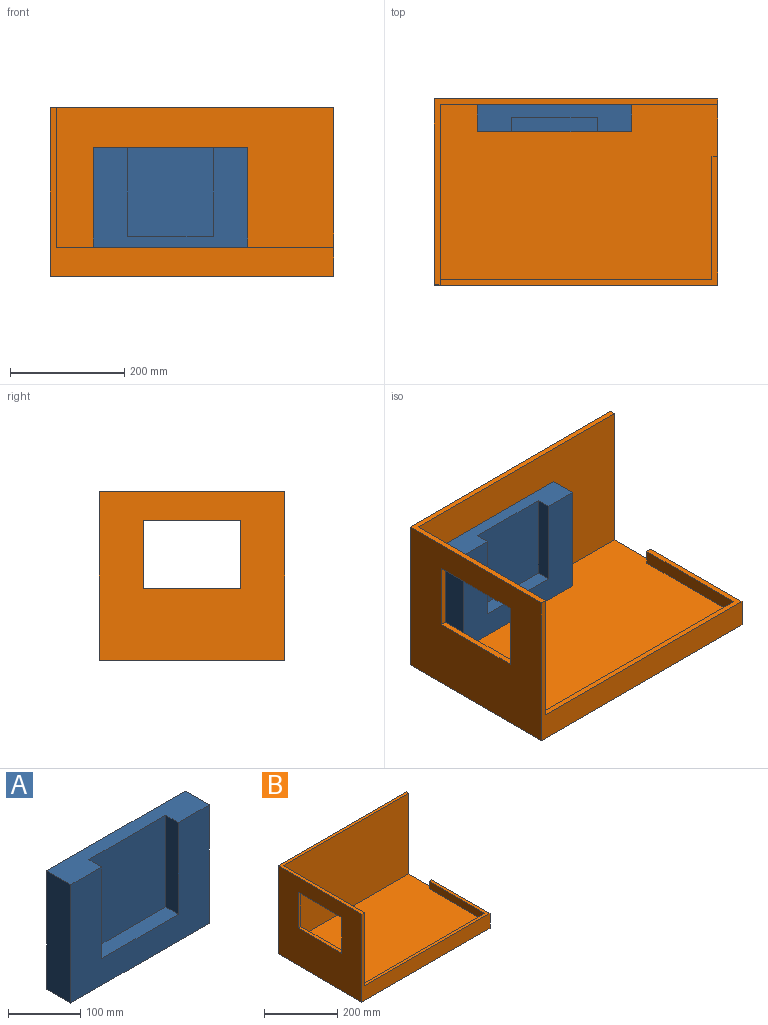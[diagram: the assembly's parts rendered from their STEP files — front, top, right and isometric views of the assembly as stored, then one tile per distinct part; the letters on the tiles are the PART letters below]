
ASSEMBLY  parts=2 mates=2
PART A: 10 faces, bbox 270x47x200 mm
  f0: plane 270x200mm, normal (0,-1,0), area 30750mm2, adj f1,f2,f4,f5,f6,f7,f8
  f1: plane 270x47mm, normal (0,0,1), area 8940mm2, adj f0,f2,f3,f4,f6,f8,f9
  f2: plane 200x47mm, normal (1,0,0), area 9400mm2, adj f0,f1,f3,f5
  f3: plane 270x200mm, normal (0,1,0), area 54000mm2, adj f1,f2,f4,f5
  f4: plane 200x47mm, normal (-1,0,0), area 9400mm2, adj f0,f1,f3,f5
  f5: plane 270x47mm, normal (0,0,-1), area 12690mm2, adj f0,f2,f3,f4
  f6: plane 155x25mm, normal (1,0,0), area 3875mm2, adj f0,f1,f7,f9
  f7: plane 150x25mm, normal (0,0,1), area 3750mm2, adj f0,f6,f8,f9
  f8: plane 155x25mm, normal (-1,0,0), area 3875mm2, adj f0,f1,f7,f9
  f9: plane 155x150mm, normal (0,-1,0), area 23250mm2, adj f1,f6,f7,f8
PART B: 17 faces, bbox 495.6x325x295 mm
  f0: plane 315x270mm, normal (1,0,0), area 64400mm2, adj f3,f4,f7,f10,f11,f12,f13,f14
  f1: plane 325x295mm, normal (-1,0,0), area 75475mm2, adj f4,f6,f9,f10,f13,f14,f15,f16
  f2: plane 215x25mm, normal (-1,0,0), area 5375mm2, adj f3,f5,f11,f12
  f3: plane 475x25mm, normal (0,1,0), area 11875mm2, adj f0,f2,f11,f12
  f4: plane 495.6x295mm, normal (0,-1,0), area 27302.8mm2, adj f0,f1,f6,f8,f10,f12
  f5: plane 25x10.3mm, normal (0,1,0), area 257.5mm2, adj f2,f8,f11,f12
  f6: plane 495.6x325mm, normal (0,0,-1), area 161068.7mm2, adj f1,f4,f8,f9
  f7: plane 485.3x270mm, normal (0,-1,0), area 131030.5mm2, adj f0,f8,f10,f11
  f8: plane 325x295mm, normal (1,0,0), area 16450mm2, adj f4,f5,f6,f7,f9,f10,f11,f12
  f9: plane 495.6x295mm, normal (0,1,0), area 146200.9mm2, adj f1,f6,f8,f10
  f10: plane 495.6x325mm, normal (0,0,1), area 8199.9mm2, adj f0,f1,f4,f7,f8,f9
  f11: plane 485.3x305mm, normal (0,0,1), area 145801.8mm2, adj f0,f2,f3,f5,f7,f8
  f12: plane 485.3x225mm, normal (0,0,1), area 7067.1mm2, adj f0,f2,f3,f4,f5,f8
  f13: plane 170x10.3mm, normal (0,0,1), area 1750.7mm2, adj f0,f1,f14,f16
  f14: plane 120x10.3mm, normal (0,-1,0), area 1235.8mm2, adj f0,f1,f13,f15
  f15: plane 170x10.3mm, normal (0,0,-1), area 1750.7mm2, adj f0,f1,f14,f16
  f16: plane 120x10.3mm, normal (0,1,0), area 1235.8mm2, adj f0,f1,f13,f15
PLACE A t=(-67.11,169.79,-35.98)mm
PLACE B t=(-29.26,40.79,-35.98)mm fixed
MATE planar A.f3 <-> B.f7  axis (0,1,0) through (-67.11,193.29,64.02)mm
MATE planar A.f5 <-> B.f11  axis (0,0,-1) through (-67.11,169.79,-35.98)mm
